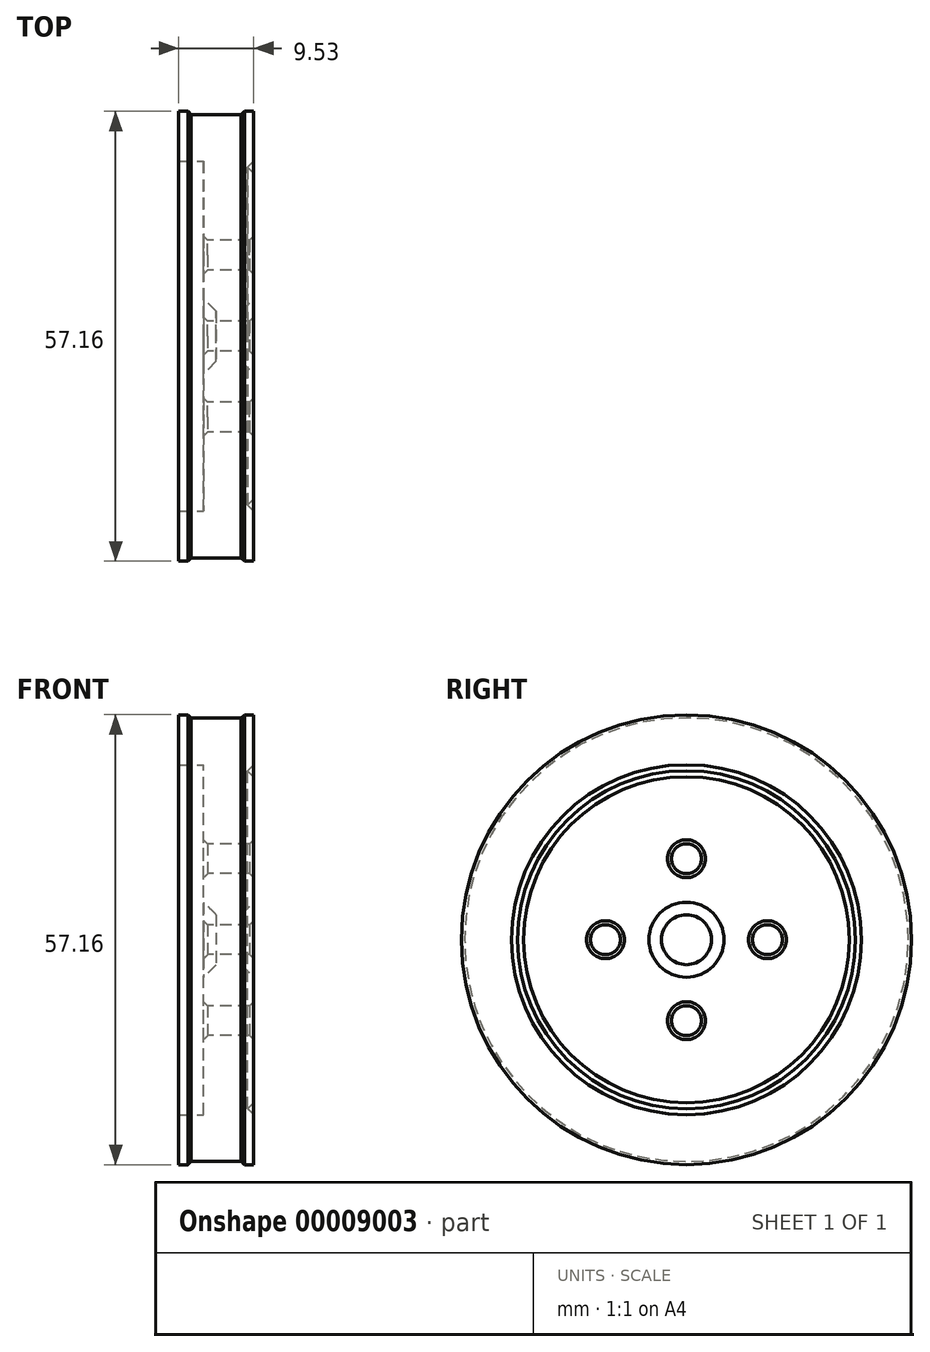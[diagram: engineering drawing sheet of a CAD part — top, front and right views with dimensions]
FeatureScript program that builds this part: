
annotation { "Feature Type Name" : "Feature", "Feature Type Description" : "" }
export const myFeature = defineFeature(function(context is Context, id is Id, definition is map)
    precondition{}
    {
        {
            var Q0;
            Q0=qCreatedBy(makeId("Front.planeOp"),FACE);
            var sketch = newSketch(context, id + "F0", { "sketchPlane" : qUnion([Q0])});
            skLineSegment(sketch, "E0", {"start": v(0, 28.58) * mm, "end": v(1.2, 28.58) * mm});
            skLineSegment(sketch, "E1", {"start": v(9.53, 0) * mm, "end": v(3.18, 0) * mm});
            skLineSegment(sketch, "E2", {"start": v(3.18, 0) * mm, "end": v(3.18, 22.23) * mm});
            skLineSegment(sketch, "E3", {"start": v(3.18, 22.23) * mm, "end": v(0, 22.23) * mm});
            skLineSegment(sketch, "E4", {"start": v(0, 22.23) * mm, "end": v(0, 28.58) * mm});
            skLineSegment(sketch, "E5", {"start": v(9.53, 28.58) * mm, "end": v(9.53, 22.23) * mm});
            skLineSegment(sketch, "E6", {"start": v(9.53, 22.23) * mm, "end": v(8.76, 21.46) * mm});
            skLineSegment(sketch, "E7", {"start": v(9.53, 20.7) * mm, "end": v(9.53, 0) * mm});
            skLineSegment(sketch, "E8", {"start": v(8.76, 21.46) * mm, "end": v(9.53, 20.7) * mm});
            skLineSegment(sketch, "E9", {"start": v(1.2, 28.58) * mm, "end": v(1.59, 28.18) * mm});
            skLineSegment(sketch, "E10", {"start": v(1.59, 28.18) * mm, "end": v(7.94, 28.18) * mm});
            skLineSegment(sketch, "E11", {"start": v(7.94, 28.18) * mm, "end": v(8.33, 28.58) * mm});
            skLineSegment(sketch, "E12.trimOffspring", {"start": v(8.33, 28.58) * mm, "end": v(9.53, 28.58) * mm});
            skSolve(sketch);
        }
        {
            var Q0;
            Q0=makeQuery(id+"F0.imprint","IMPRINT",FACE,{"disambiguationData":[TD([[makeQuery(id+"F0.imprint","IMPRINT",EDGE,{"derivedFrom":sQuery(id+"F0.wireOp",EDGE,"E0")}),-1.0]])]});
            var Q1;
            Q1=sQuery(id+"F0.wireOp",EDGE,"E1");
            revolve(context, id + "F1", {"entities" : qUnion([Q0]), "axis" : qUnion([Q1]), "revolveType" : RevolveType.FULL});
        }
        {
            var Q0;
            Q0=qCreatedBy(makeId("Right.planeOp"),FACE);
            var sketch = newSketch(context, id + "F2", { "sketchPlane" : qUnion([Q0])});
            skCircle(sketch, "E13", {"center": v(0, 10.29) * mm, "radius": 1.9 * mm});
            skCircle(sketch, "E14.1.0", {"center": v(-10.29, 0) * mm, "radius": 1.9 * mm});
            skCircle(sketch, "E14.2.0", {"center": v(0, -10.29) * mm, "radius": 1.9 * mm});
            skCircle(sketch, "E14.3.0", {"center": v(10.29, 0) * mm, "radius": 1.9 * mm});
            skPoint(sketch, "E14.center", {"position": v(0, 0) * mm});
            skSolve(sketch);
        }
        {
            var Q0;
            Q0 = qSketchRegion(id + "F2", true);
            extrude(context, id + "F3", {"entities" : qUnion([Q0]), "operationType" : NewBodyOperationType.REMOVE, "endBound" : BoundingType.THROUGH_ALL, "depth" : 25.4 * mm});
        }
        {
            var Q0;
            Q0=makeQuery(id+"F1.opRevolve","SWEPT_FACE",FACE,{"disambiguationData":[OSD([sQuery(id+"F0.wireOp",EDGE,"E2")])]});
            var sketch = newSketch(context, id + "F4", { "sketchPlane" : qUnion([Q0])});
            skCircle(sketch, "E15", {"center": v(0, 0) * mm, "radius": 4.76 * mm});
            skSolve(sketch);
        }
        {
            var Q0;
            Q0 = qSketchRegion(id + "F4", true);
            extrude(context, id + "F5", {"entities" : qUnion([Q0]), "operationType" : NewBodyOperationType.REMOVE, "oppositeDirection" : true, "depth" : 1.59 * mm});
        }
        {
            var Q0;
            Q0=makeQuery(id+"F5.boolean.opBoolean","COPY",EDGE,{"derivedFrom":makeQuery(id+"F5.opExtrude","CAP_EDGE",EDGE,{"disambiguationData":[OSD([sQuery(id+"F4.wireOp",EDGE,"E15")])],"isStart":false})});
            chamfer(context, id + "F6", {"entities" : qUnion([Q0]), "width" : 1.59 * mm, "tangentPropagation" : true});
        }
        {
            var Q0;
            Q0=makeQuery(id+"F3.boolean.opBoolean","COPY",FACE,{"derivedFrom":makeQuery(id+"F3.opExtrude","SWEPT_FACE",FACE,{"disambiguationData":[OSD([sQuery(id+"F2.wireOp",EDGE,"E14.3.0")])]})});
            var Q1;
            Q1=makeQuery(id+"F3.boolean.opBoolean","COPY",FACE,{"derivedFrom":makeQuery(id+"F3.opExtrude","SWEPT_FACE",FACE,{"disambiguationData":[OSD([sQuery(id+"F2.wireOp",EDGE,"E13")])]})});
            var Q2;
            Q2=makeQuery(id+"F3.boolean.opBoolean","COPY",FACE,{"derivedFrom":makeQuery(id+"F3.opExtrude","SWEPT_FACE",FACE,{"disambiguationData":[OSD([sQuery(id+"F2.wireOp",EDGE,"E14.1.0")])]})});
            var Q3;
            Q3=makeQuery(id+"F3.boolean.opBoolean","COPY",FACE,{"derivedFrom":makeQuery(id+"F3.opExtrude","SWEPT_FACE",FACE,{"disambiguationData":[OSD([sQuery(id+"F2.wireOp",EDGE,"E14.2.0")])]})});
            chamfer(context, id + "F7", {"entities" : qUnion([Q0, Q1, Q2, Q3]), "width" : 0.5 * mm, "tangentPropagation" : true});
        }
        {
            var Q0;
            Q0=makeQuery(id+"F1.opRevolve","SWEPT_FACE",FACE,{"disambiguationData":[OSD([sQuery(id+"F0.wireOp",EDGE,"E7")])]});
            var sketch = newSketch(context, id + "F8", { "sketchPlane" : qUnion([Q0])});
            skCircle(sketch, "E16", {"center": v(0, 0) * mm, "radius": 4.76 * mm});
            skSolve(sketch);
        }
        {
            var Q0;
            Q0=makeQuery(id+"F8.imprint","IMPRINT",FACE,{"disambiguationData":[TD([[makeQuery(id+"F8.imprint","IMPRINT",EDGE,{"derivedFrom":sQuery(id+"F8.wireOp",EDGE,"E16")}),1.0]])]});
            extrude(context, id + "F9", {"entities" : qUnion([Q0]), "operationType" : NewBodyOperationType.REMOVE, "oppositeDirection" : true, "depth" : 1.59 * mm});
        }
        {
            var Q0;
            Q0=makeQuery(id+"F9.boolean.opBoolean","COPY",EDGE,{"derivedFrom":makeQuery(id+"F9.opExtrude","CAP_EDGE",EDGE,{"disambiguationData":[OSD([sQuery(id+"F8.wireOp",EDGE,"E16")])],"isStart":false})});
            chamfer(context, id + "F10", {"entities" : qUnion([Q0]), "width" : 1.59 * mm, "tangentPropagation" : true});
        }
    });
